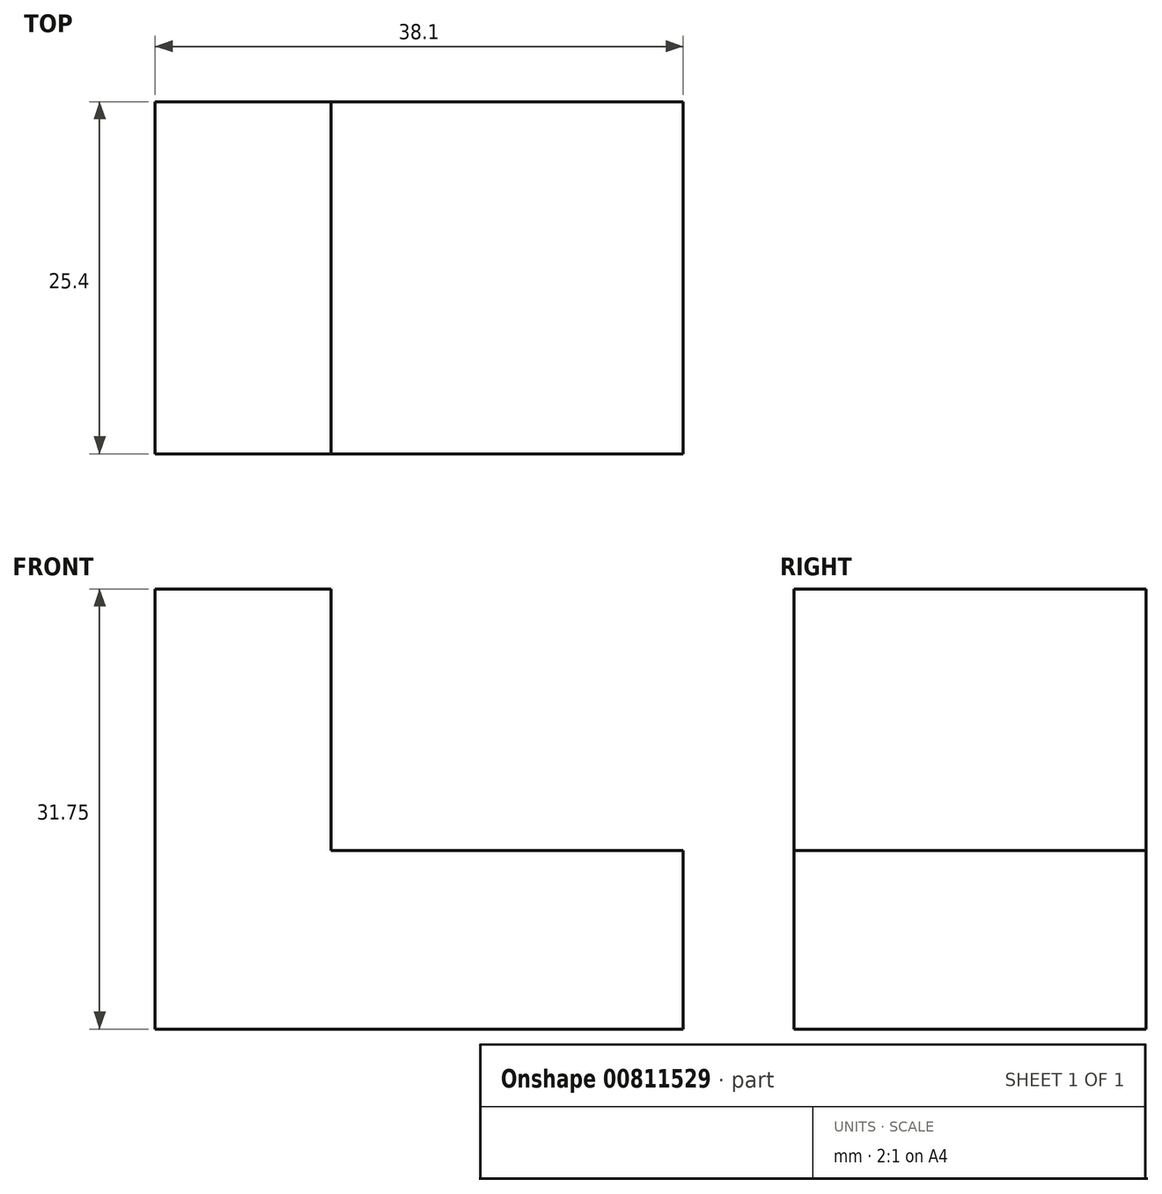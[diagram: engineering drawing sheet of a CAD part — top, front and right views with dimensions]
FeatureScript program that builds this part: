
annotation { "Feature Type Name" : "Feature", "Feature Type Description" : "" }
export const myFeature = defineFeature(function(context is Context, id is Id, definition is map)
    precondition{}
    {
        {
            var Q0;
            Q0=qCreatedBy(makeId("Front.planeOp"),FACE);
            var sketch = newSketch(context, id + "F0", { "sketchPlane" : qUnion([Q0])});
            skLineSegment(sketch, "E0", {"start": v(0, 0) * mm, "end": v(38.1, 0) * mm});
            skLineSegment(sketch, "E1", {"start": v(0, 0) * mm, "end": v(0, 31.75) * mm});
            skLineSegment(sketch, "E2", {"start": v(0, 31.75) * mm, "end": v(12.7, 31.75) * mm});
            skLineSegment(sketch, "E3", {"start": v(12.7, 31.75) * mm, "end": v(12.7, 12.87) * mm});
            skLineSegment(sketch, "E4", {"start": v(12.7, 12.87) * mm, "end": v(38.1, 12.87) * mm});
            skLineSegment(sketch, "E5", {"start": v(38.1, 12.87) * mm, "end": v(38.1, 0) * mm});
            skSolve(sketch);
        }
        {
            var Q0;
            Q0=makeQuery(id+"F0.imprint","IMPRINT",FACE,{"disambiguationData":[TD([[makeQuery(id+"F0.imprint","IMPRINT",EDGE,{"derivedFrom":sQuery(id+"F0.wireOp",EDGE,"E0")}),1.0]])]});
            extrude(context, id + "F1", {"entities" : qUnion([Q0]), "depth" : 25.4 * mm, "offsetDistance" : 25.4 * mm});
        }
    });
